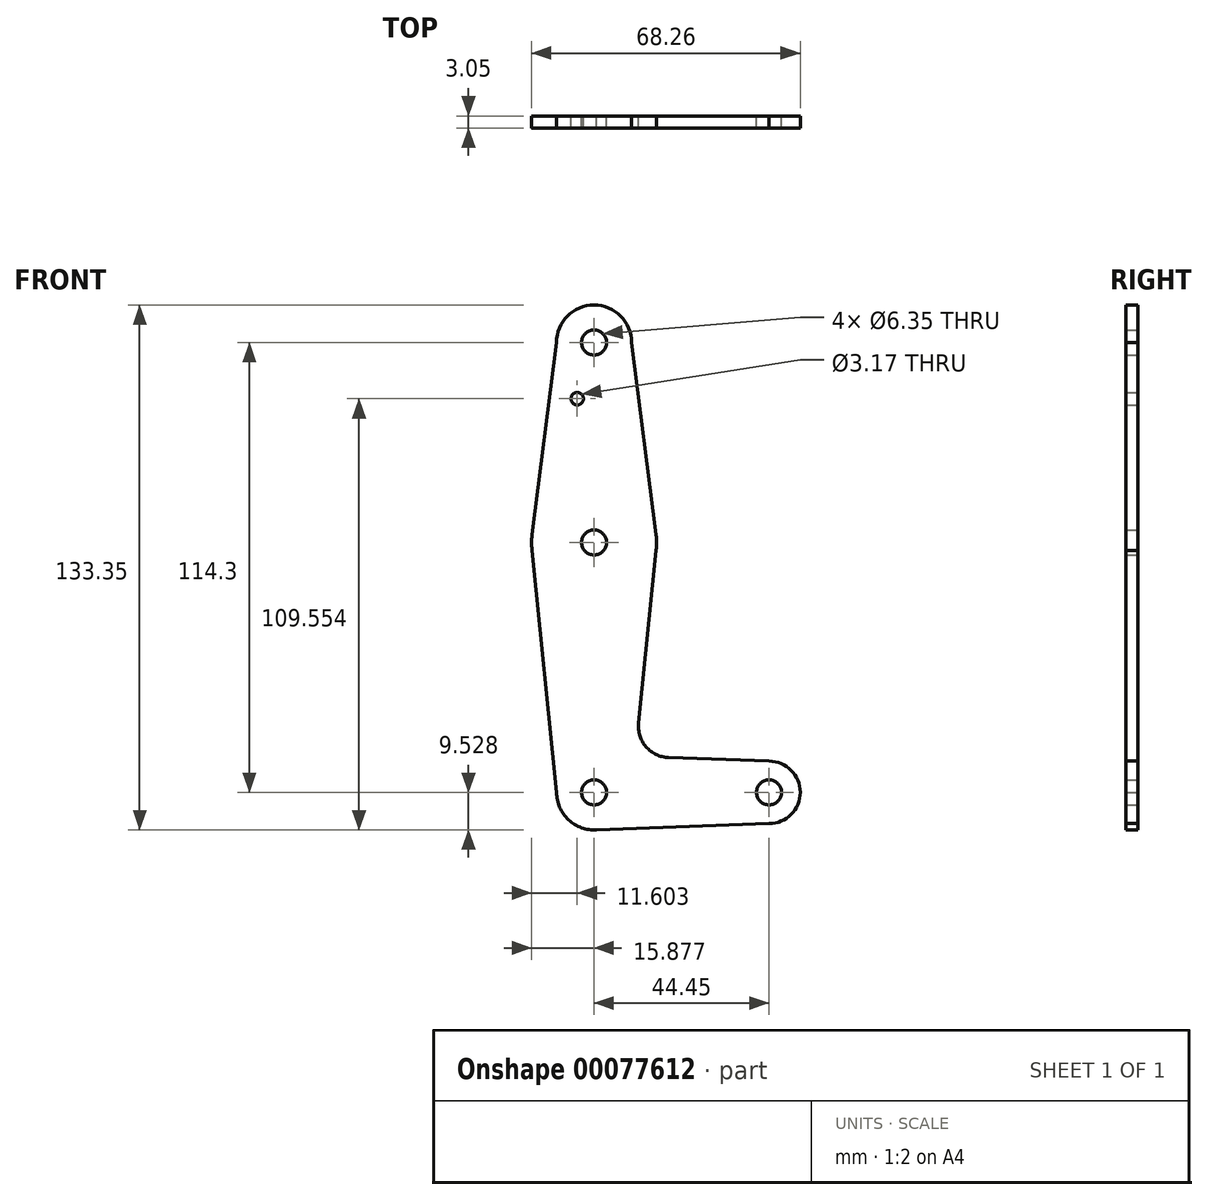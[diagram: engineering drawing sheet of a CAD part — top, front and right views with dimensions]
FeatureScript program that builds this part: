
annotation { "Feature Type Name" : "Feature", "Feature Type Description" : "" }
export const myFeature = defineFeature(function(context is Context, id is Id, definition is map)
    precondition{}
    {
        {
            var Q0;
            Q0=qCreatedBy(makeId("Front.planeOp"),FACE);
            var sketch = newSketch(context, id + "F0", { "sketchPlane" : qUnion([Q0])});
            skLineSegment(sketch, "E0", {"start": v(-81.08, 82.93) * mm, "end": v(-81.08, -31.37) * mm});
            skLineSegment(sketch, "E1", {"start": v(-81.08, -31.37) * mm, "end": v(-36.63, -31.37) * mm});
            skCircle(sketch, "E2", {"center": v(-81.08, 82.93) * mm, "radius": 9.53 * mm});
            skCircle(sketch, "E3", {"center": v(-81.08, 32.13) * mm, "radius": 15.88 * mm});
            skCircle(sketch, "E4", {"center": v(-81.08, -31.37) * mm, "radius": 9.53 * mm});
            skCircle(sketch, "E5", {"center": v(-36.63, -31.37) * mm, "radius": 7.94 * mm});
            skLineSegment(sketch, "E6", {"start": v(-71.56, 82.93) * mm, "end": v(-65.34, 34.14) * mm});
            skLineSegment(sketch, "E7", {"start": v(-65.34, 30.12) * mm, "end": v(-69.78, -13.78) * mm});
            skLineSegment(sketch, "E8", {"start": v(-90.6, 82.93) * mm, "end": v(-96.83, 34.14) * mm});
            skLineSegment(sketch, "E9", {"start": v(-96.83, 30.12) * mm, "end": v(-90.6, -31.37) * mm});
            skLineSegment(sketch, "E10", {"start": v(-81.08, -40.9) * mm, "end": v(-36.63, -39.3) * mm});
            skLineSegment(sketch, "E11", {"start": v(-62.15, -22.52) * mm, "end": v(-36.63, -23.43) * mm});
            skCircle(sketch, "E12", {"center": v(-85.36, 68.65) * mm, "radius": 1.59 * mm});
            skCircle(sketch, "E13", {"center": v(-81.08, 82.93) * mm, "radius": 3.18 * mm});
            skCircle(sketch, "E14", {"center": v(-81.08, 32.13) * mm, "radius": 3.18 * mm});
            skCircle(sketch, "E15", {"center": v(-81.08, -31.37) * mm, "radius": 3.18 * mm});
            skCircle(sketch, "E16", {"center": v(-36.63, -31.37) * mm, "radius": 3.18 * mm});
            skArc(sketch, "E17.filletArc", {"start": v(-69.78, -13.78) * mm, "mid": v(-67.86, -19.8) * mm, "end": v(-62.15, -22.52) * mm});
            skSolve(sketch);
        }
        {
            var Q0;
            Q0 = qSketchRegion(id + "F0", true);
            var Q1;
            {var subQ0=sQuery(id+"F0.wireOp",EDGE,"E4");var subQ1=sQuery(id+"F0.wireOp",EDGE,"E0");var subQ2=makeQuery(id+"F0.imprint","INTERSECT",VERTEX,{"derivedFrom":[subQ1,subQ0]});Q1=makeQuery(id+"F0.imprint","IMPRINT",FACE,{"disambiguationData":[TD([[makeQuery(id+"F0.imprint","IMPRINT",EDGE,{"disambiguationData":[TD([[subQ2,-1.0]])],"derivedFrom":subQ1}),1.0]])]});}
            extrude(context, id + "F1", {"entities" : qUnion([Q0, Q1]), "depth" : 3.05 * mm});
        }
    });
